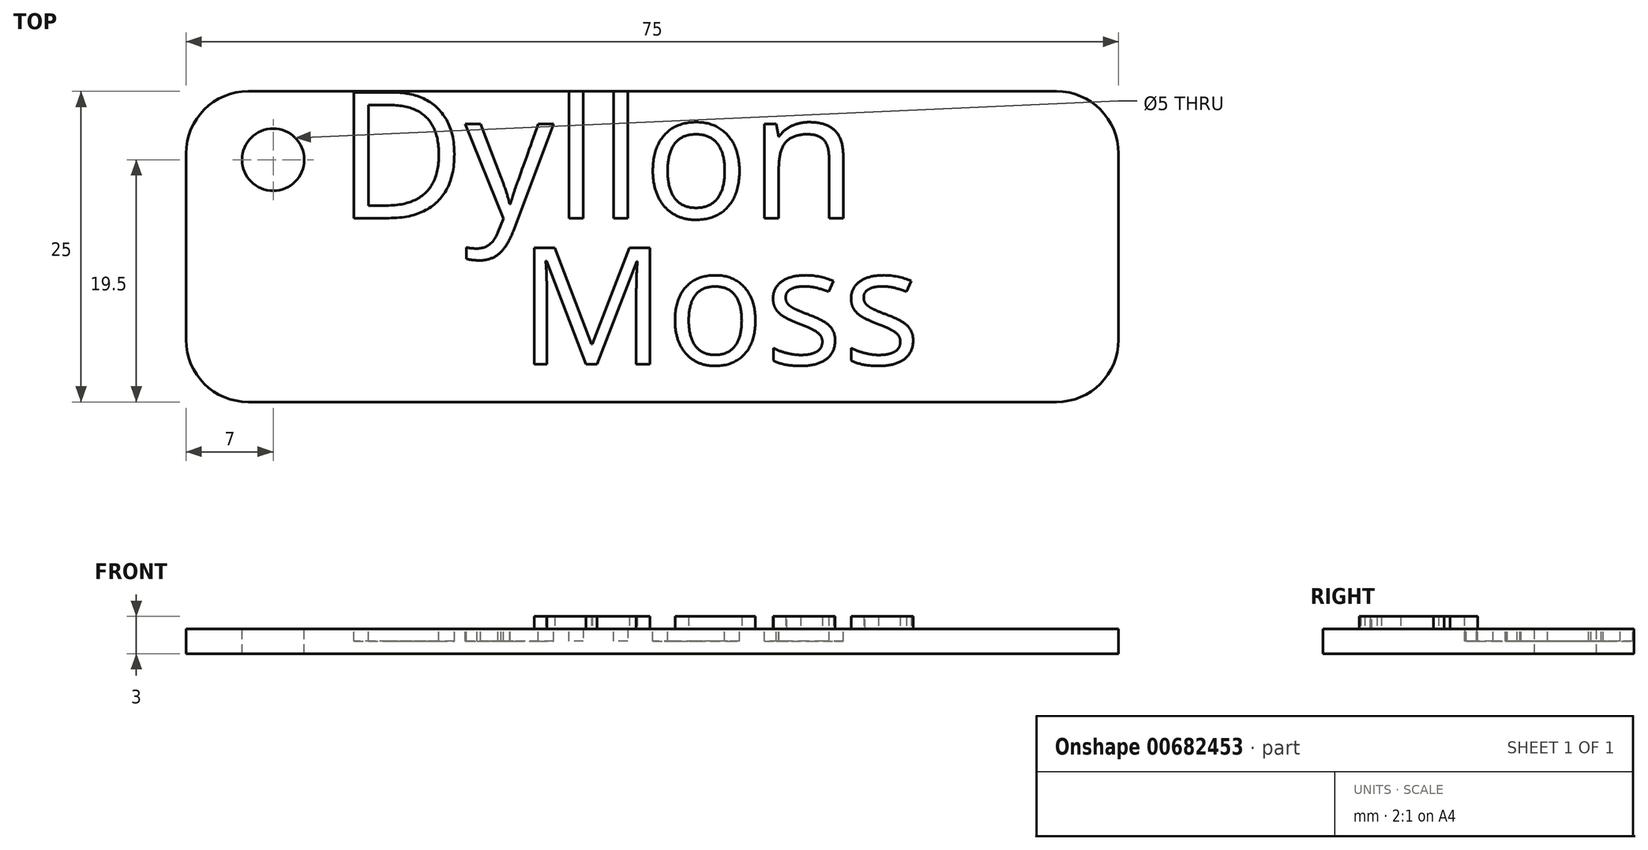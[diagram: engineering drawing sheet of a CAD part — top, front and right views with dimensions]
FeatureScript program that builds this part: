
annotation { "Feature Type Name" : "Feature", "Feature Type Description" : "" }
export const myFeature = defineFeature(function(context is Context, id is Id, definition is map)
    precondition{}
    {
        {
            var Q0;
            Q0=qCreatedBy(makeId("Top.planeOp"),FACE);
            var sketch = newSketch(context, id + "F0", { "sketchPlane" : qUnion([Q0])});
            skLineSegment(sketch, "E0.bottom", {"start": v(32.5, 12.5) * mm, "end": v(-32.5, 12.5) * mm});
            skLineSegment(sketch, "E0.top", {"start": v(32.5, -12.5) * mm, "end": v(-32.5, -12.5) * mm});
            skLineSegment(sketch, "E0.left", {"start": v(37.5, 7.5) * mm, "end": v(37.5, -7.5) * mm});
            skLineSegment(sketch, "E0.right", {"start": v(-37.5, 7.5) * mm, "end": v(-37.5, -7.5) * mm});
            skPoint(sketch, "E0.middle", {"position": v(0, 0) * mm});
            skPoint(sketch, "E1.visualSharp", {"position": v(-37.5, 12.5) * mm});
            skArc(sketch, "E1.filletArc", {"start": v(-32.5, 12.5) * mm, "mid": v(-36.04, 11.04) * mm, "end": v(-37.5, 7.5) * mm});
            skPoint(sketch, "E2.visualSharp", {"position": v(-37.5, -12.5) * mm});
            skArc(sketch, "E2.filletArc", {"start": v(-37.5, -7.5) * mm, "mid": v(-36.04, -11.04) * mm, "end": v(-32.5, -12.5) * mm});
            skPoint(sketch, "E3.visualSharp", {"position": v(37.5, 12.5) * mm});
            skArc(sketch, "E3.filletArc", {"start": v(37.5, 7.5) * mm, "mid": v(36.04, 11.04) * mm, "end": v(32.5, 12.5) * mm});
            skPoint(sketch, "E4.visualSharp", {"position": v(37.5, -12.5) * mm});
            skArc(sketch, "E4.filletArc", {"start": v(32.5, -12.5) * mm, "mid": v(36.04, -11.04) * mm, "end": v(37.5, -7.5) * mm});
            skSolve(sketch);
        }
        {
            var Q0;
            Q0=makeQuery(id+"F0.imprint","IMPRINT",FACE,{"disambiguationData":[TD([[makeQuery(id+"F0.imprint","IMPRINT",EDGE,{"derivedFrom":sQuery(id+"F0.wireOp",EDGE,"E0.bottom")}),1.0]])]});
            extrude(context, id + "F1", {"entities" : qUnion([Q0]), "depth" : 2 * mm, "offsetDistance" : 25 * mm});
        }
        {
            var Q0;
            Q0=makeQuery(id+"F1.opExtrude","CAP_FACE",FACE,{"disambiguationData":[OSD([sQuery(id+"F0.wireOp",EDGE,"E0.bottom"),sQuery(id+"F0.wireOp",EDGE,"E0.top"),sQuery(id+"F0.wireOp",EDGE,"E0.left"),sQuery(id+"F0.wireOp",EDGE,"E0.right"),sQuery(id+"F0.wireOp",EDGE,"E1.filletArc"),sQuery(id+"F0.wireOp",EDGE,"E2.filletArc"),sQuery(id+"F0.wireOp",EDGE,"E3.filletArc"),sQuery(id+"F0.wireOp",EDGE,"E4.filletArc")])],"isStart":false});
            var sketch = newSketch(context, id + "F2", { "sketchPlane" : qUnion([Q0])});
            skPoint(sketch, "E5", {"position": v(-30.5, 7) * mm});
            skSolve(sketch);
        }
        {
            var Q0;
            Q0=sQuery(id+"F2.wireOp",VERTEX,"E5");
            var Q1;
            Q1=makeQuery(id+"F1.opExtrude","SWEPT_BODY",BODY,{"disambiguationData":[OSD([sQuery(id+"F0.wireOp",EDGE,"E0.bottom"),sQuery(id+"F0.wireOp",EDGE,"E0.top"),sQuery(id+"F0.wireOp",EDGE,"E0.left"),sQuery(id+"F0.wireOp",EDGE,"E0.right"),sQuery(id+"F0.wireOp",EDGE,"E1.filletArc"),sQuery(id+"F0.wireOp",EDGE,"E2.filletArc"),sQuery(id+"F0.wireOp",EDGE,"E3.filletArc"),sQuery(id+"F0.wireOp",EDGE,"E4.filletArc")])]});
            hole(context, id + "F3", {"style" : HoleStyle.SIMPLE, "endStyle" : HoleEndStyle.THROUGH, "holeDiameter" : 5 * mm, "majorDiameter" : 5 * mm, "isTappedThrough" : true, "tappedDepth" : 12 * mm, "tapClearance" : 3, "locations" : qUnion([Q0]), "scope" : qUnion([Q1])});
        }
        {
            var Q0;
            Q0=makeQuery(id+"F1.opExtrude","CAP_FACE",FACE,{"disambiguationData":[OSD([sQuery(id+"F0.wireOp",EDGE,"E0.bottom"),sQuery(id+"F0.wireOp",EDGE,"E0.top"),sQuery(id+"F0.wireOp",EDGE,"E0.left"),sQuery(id+"F0.wireOp",EDGE,"E0.right"),sQuery(id+"F0.wireOp",EDGE,"E1.filletArc"),sQuery(id+"F0.wireOp",EDGE,"E2.filletArc"),sQuery(id+"F0.wireOp",EDGE,"E3.filletArc"),sQuery(id+"F0.wireOp",EDGE,"E4.filletArc")])],"isStart":false});
            var sketch = newSketch(context, id + "F4", { "sketchPlane" : qUnion([Q0])});
            skText(sketch, "E6", { "text": "Dyllon", "fontName": "OpenSans-Regular.ttf"});
            const initialGuessF4  = {"E6": [-0.02539, 0.0023, 1, 0, 0.0102]};
            skSetInitialGuess(sketch, initialGuessF4);
            skSolve(sketch);
        }
        {
            var Q0;
            Q0 = qSketchRegion(id + "F4", true);
            extrude(context, id + "F5", {"entities" : qUnion([Q0]), "operationType" : NewBodyOperationType.REMOVE, "oppositeDirection" : true, "depth" : 1 * mm, "offsetDistance" : 25 * mm});
        }
        {
            var Q0;
            {var subQ0=sQuery(id+"F0.wireOp",EDGE,"E1.filletArc");var subQ1=sQuery(id+"F0.wireOp",EDGE,"E0.right");var subQ2=sQuery(id+"F0.wireOp",EDGE,"E0.top");var subQ3=sQuery(id+"F0.wireOp",EDGE,"E0.bottom");var subQ4=sQuery(id+"F0.wireOp",EDGE,"E2.filletArc");var subQ5=sQuery(id+"F0.wireOp",EDGE,"E4.filletArc");var subQ6=sQuery(id+"F0.wireOp",EDGE,"E3.filletArc");var subQ7=sQuery(id+"F0.wireOp",EDGE,"E0.left");Q0=makeQuery(id+"F5.boolean.opBoolean","SPLIT",FACE,{"disambiguationData":[TD([makeQuery(id+"F1.opExtrude","SWEPT_FACE",FACE,{"disambiguationData":[OSD([subQ3])]})])],"derivedFrom":makeQuery(id+"F1.opExtrude","CAP_FACE",FACE,{"disambiguationData":[OSD([subQ3,subQ2,subQ7,subQ1,subQ0,subQ4,subQ6,subQ5])],"isStart":false})});}
            var sketch = newSketch(context, id + "F6", { "sketchPlane" : qUnion([Q0])});
            skText(sketch, "E7", { "text": "Moss", "fontName": "OpenSans-Regular.ttf"});
            const initialGuessF6  = {"E7": [-0.01079, -0.00947, 1, 0, 0.00947]};
            skSetInitialGuess(sketch, initialGuessF6);
            skSolve(sketch);
        }
        {
            var Q0;
            Q0 = qSketchRegion(id + "F6", true);
            extrude(context, id + "F7", {"entities" : qUnion([Q0]), "operationType" : NewBodyOperationType.ADD, "depth" : 1 * mm, "offsetDistance" : 25 * mm});
        }
    });
